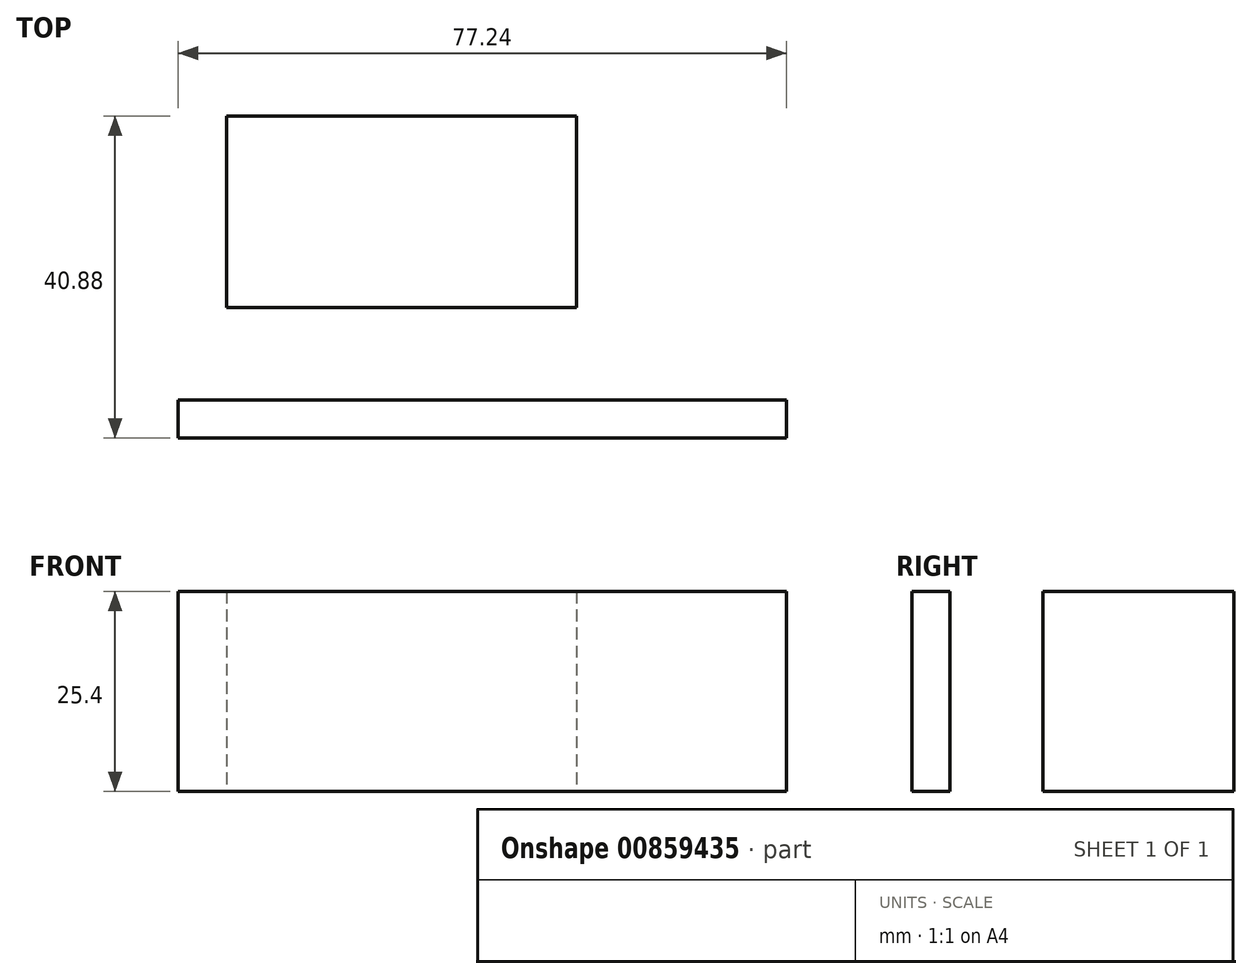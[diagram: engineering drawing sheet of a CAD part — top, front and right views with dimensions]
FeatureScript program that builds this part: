
annotation { "Feature Type Name" : "Feature", "Feature Type Description" : "" }
export const myFeature = defineFeature(function(context is Context, id is Id, definition is map)
    precondition{}
    {
        {
            var Q0;
            Q0=qCreatedBy(makeId("Top.planeOp"),FACE);
            var sketch = newSketch(context, id + "F0", { "sketchPlane" : qUnion([Q0])});
            skLineSegment(sketch, "E0.bottom", {"start": v(-60.74, 0) * mm, "end": v(-16.3, 0) * mm});
            skLineSegment(sketch, "E0.top", {"start": v(-60.74, -24.3) * mm, "end": v(-16.3, -24.3) * mm});
            skLineSegment(sketch, "E0.left", {"start": v(-60.74, 0) * mm, "end": v(-60.74, -24.3) * mm});
            skLineSegment(sketch, "E0.right", {"start": v(-16.3, 0) * mm, "end": v(-16.3, -24.3) * mm});
            skLineSegment(sketch, "E1.bottom", {"start": v(10.35, -40.88) * mm, "end": v(-66.9, -40.88) * mm});
            skLineSegment(sketch, "E1.top", {"start": v(10.35, -36.08) * mm, "end": v(-66.9, -36.08) * mm});
            skLineSegment(sketch, "E1.left", {"start": v(10.35, -40.88) * mm, "end": v(10.35, -36.08) * mm});
            skLineSegment(sketch, "E1.right", {"start": v(-66.9, -40.88) * mm, "end": v(-66.9, -36.08) * mm});
            skSolve(sketch);
        }
        {
            var Q0;
            Q0 = qSketchRegion(id + "F0", true);
            extrude(context, id + "F1", {"entities" : qUnion([Q0]), "depth" : 25.4 * mm, "offsetDistance" : 25.4 * mm});
        }
    });
